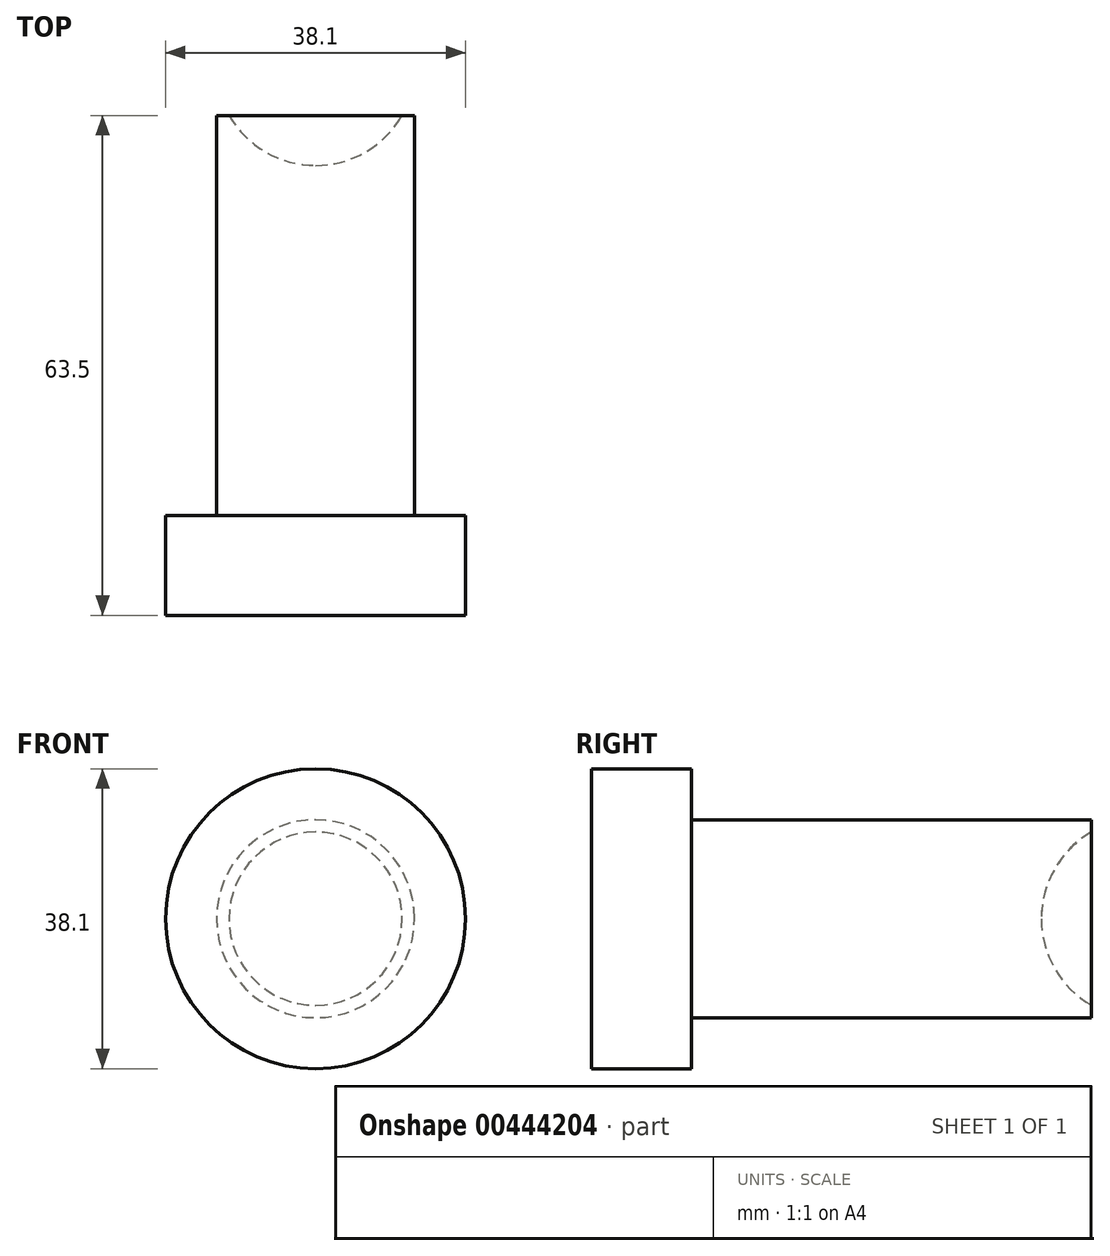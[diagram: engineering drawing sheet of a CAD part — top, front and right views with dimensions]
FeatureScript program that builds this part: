
annotation { "Feature Type Name" : "Feature", "Feature Type Description" : "" }
export const myFeature = defineFeature(function(context is Context, id is Id, definition is map)
    precondition{}
    {
        {
            var Q0;
            Q0=qCreatedBy(makeId("Front.planeOp"),FACE);
            var sketch = newSketch(context, id + "F0", { "sketchPlane" : qUnion([Q0])});
            skCircle(sketch, "E0", {"center": v(0, 0) * mm, "radius": 19.05 * mm});
            skCircle(sketch, "E1", {"center": v(0, 0) * mm, "radius": 12.57 * mm});
            skSolve(sketch);
        }
        {
            var Q0;
            Q0=makeQuery(id+"F0.imprint","IMPRINT",FACE,{"disambiguationData":[TD([[makeQuery(id+"F0.imprint","IMPRINT",EDGE,{"derivedFrom":sQuery(id+"F0.wireOp",EDGE,"E0")}),1.0]])]});
            var Q1;
            Q1=makeQuery(id+"F0.imprint","IMPRINT",FACE,{"disambiguationData":[TD([[makeQuery(id+"F0.imprint","IMPRINT",EDGE,{"derivedFrom":sQuery(id+"F0.wireOp",EDGE,"E1")}),1.0]])]});
            extrude(context, id + "F1", {"entities" : qUnion([Q0, Q1]), "oppositeDirection" : true, "depth" : 12.7 * mm});
        }
        {
            var Q0;
            Q0=makeQuery(id+"F0.imprint","IMPRINT",FACE,{"disambiguationData":[TD([[makeQuery(id+"F0.imprint","IMPRINT",EDGE,{"derivedFrom":sQuery(id+"F0.wireOp",EDGE,"E1")}),1.0]])]});
            extrude(context, id + "F2", {"entities" : qUnion([Q0]), "operationType" : NewBodyOperationType.ADD, "oppositeDirection" : true, "depth" : 63.5 * mm});
        }
        {
            var Q0;
            Q0=qCreatedBy(makeId("Right.planeOp"),FACE);
            var sketch = newSketch(context, id + "F3", { "sketchPlane" : qUnion([Q0])});
            skLineSegment(sketch, "E2", {"start": v(69.85, 15.85) * mm, "end": v(69.85, -17.45) * mm});
            skArc(sketch, "E3", {"start": v(69.85, 12.7) * mm, "mid": v(57.15, 0) * mm, "end": v(69.85, -12.7) * mm});
            skLineSegment(sketch, "E4", {"start": v(75.88, 0) * mm, "end": v(52.83, 0) * mm});
            skPoint(sketch, "E4.endSnap0", {"position": v(57.15, 0) * mm});
            skSolve(sketch);
        }
        {
            var Q0;
            {var subQ0=sQuery(id+"F3.wireOp",EDGE,"E3");var subQ1=sQuery(id+"F3.wireOp",EDGE,"E2");var subQ2=makeQuery(id+"F3.imprint","INTERSECT",VERTEX,{"disambiguationData":[OD(0.0)],"derivedFrom":[subQ1,subQ0]});Q0=makeQuery(id+"F3.imprint","IMPRINT",FACE,{"disambiguationData":[TD([[makeQuery(id+"F3.imprint","IMPRINT",EDGE,{"disambiguationData":[TD([[subQ2,-1.0]])],"derivedFrom":subQ1}),-1.0]])]});}
            var Q1;
            Q1=sQuery(id+"F3.wireOp",EDGE,"E4");
            revolve(context, id + "F4", {"operationType" : NewBodyOperationType.REMOVE, "entities" : qUnion([Q0]), "axis" : qUnion([Q1]), "revolveType" : RevolveType.FULL, "oppositeDirection" : true});
        }
    });
